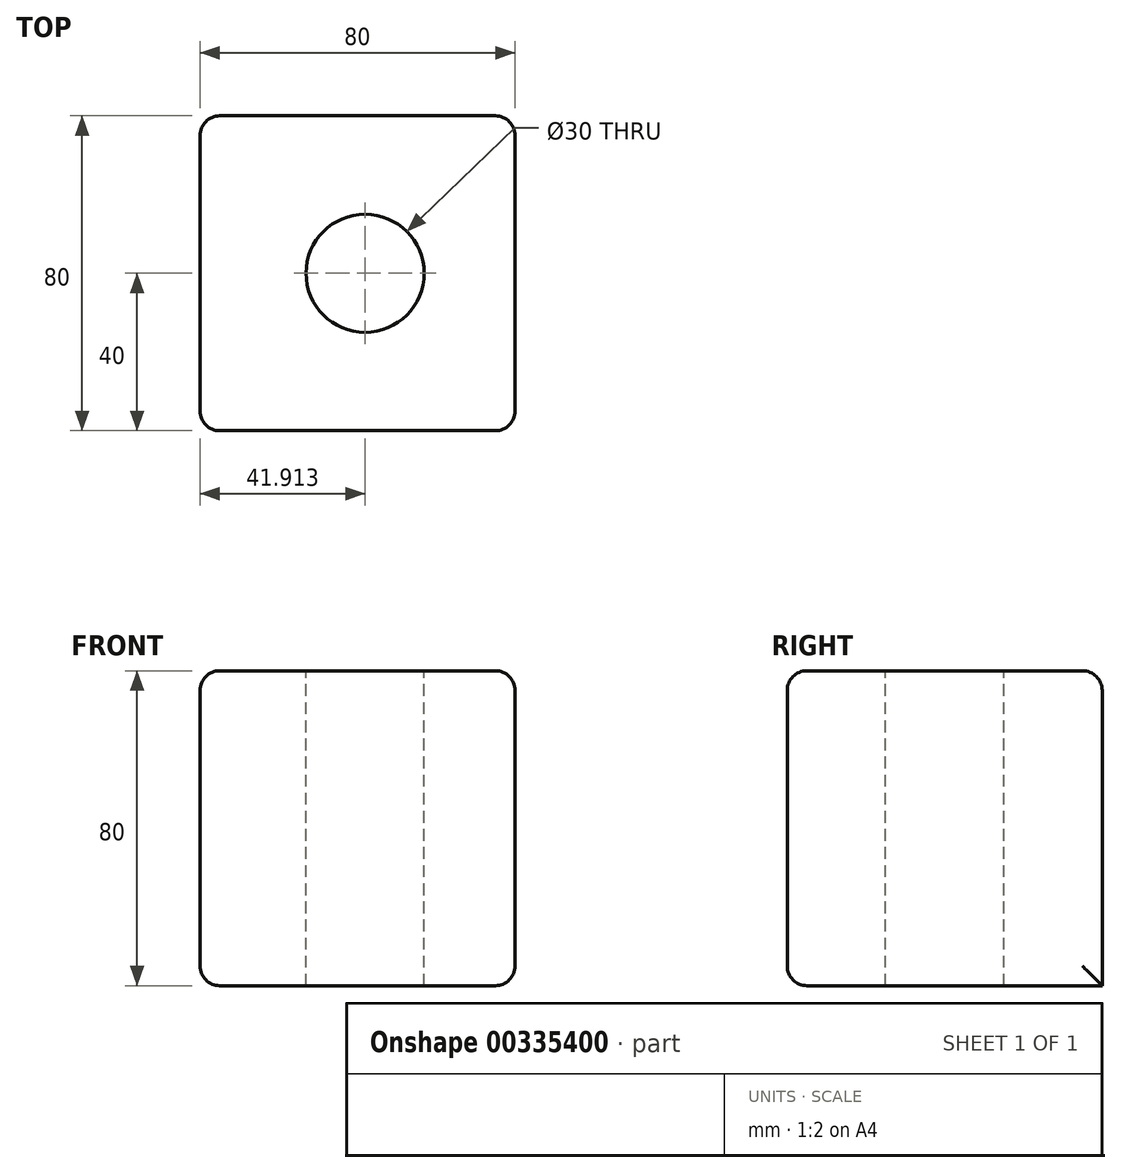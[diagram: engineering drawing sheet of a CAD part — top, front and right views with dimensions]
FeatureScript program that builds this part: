
annotation { "Feature Type Name" : "Feature", "Feature Type Description" : "" }
export const myFeature = defineFeature(function(context is Context, id is Id, definition is map)
    precondition{}
    {
        {
            var Q0;
            Q0=qCreatedBy(makeId("Top.planeOp"),FACE);
            var sketch = newSketch(context, id + "F0", { "sketchPlane" : qUnion([Q0])});
            skLineSegment(sketch, "E0.bottom", {"start": v(40, -40) * mm, "end": v(-40, -40) * mm});
            skLineSegment(sketch, "E0.top", {"start": v(40, 40) * mm, "end": v(-40, 40) * mm});
            skLineSegment(sketch, "E0.left", {"start": v(40, -40) * mm, "end": v(40, 40) * mm});
            skLineSegment(sketch, "E0.right", {"start": v(-40, -40) * mm, "end": v(-40, 40) * mm});
            skPoint(sketch, "E0.middle", {"position": v(0, 0) * mm});
            skSolve(sketch);
        }
        {
            var Q0;
            Q0=makeQuery(id+"F0.imprint","IMPRINT",FACE,{"disambiguationData":[TD([[makeQuery(id+"F0.imprint","IMPRINT",EDGE,{"derivedFrom":sQuery(id+"F0.wireOp",EDGE,"E0.bottom")}),-1.0]])]});
            extrude(context, id + "F1", {"entities" : qUnion([Q0]), "endBound" : BoundingType.SYMMETRIC, "depth" : 80 * mm});
        }
        {
            var Q0;
            Q0=makeQuery(id+"F1.opExtrude","CAP_EDGE",EDGE,{"disambiguationData":[OSD([sQuery(id+"F0.wireOp",EDGE,"E0.right")])],"isStart":false});
            var Q1;
            Q1=makeQuery(id+"F1.opExtrude","CAP_EDGE",EDGE,{"disambiguationData":[OSD([sQuery(id+"F0.wireOp",EDGE,"E0.right")])],"isStart":true});
            var Q2;
            Q2=makeQuery(id+"F1.opExtrude","CAP_EDGE",EDGE,{"disambiguationData":[OSD([sQuery(id+"F0.wireOp",EDGE,"E0.top")])],"isStart":false});
            var Q3;
            Q3=makeQuery(id+"F1.opExtrude","CAP_EDGE",EDGE,{"disambiguationData":[OSD([sQuery(id+"F0.wireOp",EDGE,"E0.bottom")])],"isStart":false});
            var Q4;
            Q4=makeQuery(id+"F1.opExtrude","SWEPT_FACE",FACE,{"disambiguationData":[OSD([sQuery(id+"F0.wireOp",EDGE,"E0.right")])]});
            var Q5;
            Q5=makeQuery(id+"F1.opExtrude","SWEPT_EDGE",EDGE,{"disambiguationData":[OSD([sQuery(id+"F0.wireOp",EDGE,"E0.bottom"),sQuery(id+"F0.wireOp",EDGE,"E0.right")])]});
            var Q6;
            Q6=makeQuery(id+"F1.opExtrude","SWEPT_EDGE",EDGE,{"disambiguationData":[OSD([sQuery(id+"F0.wireOp",EDGE,"E0.top"),sQuery(id+"F0.wireOp",EDGE,"E0.right")])]});
            var Q7;
            Q7=makeQuery(id+"F1.opExtrude","CAP_EDGE",EDGE,{"disambiguationData":[OSD([sQuery(id+"F0.wireOp",EDGE,"E0.left")])],"isStart":true});
            var Q8;
            Q8=makeQuery(id+"F1.opExtrude","SWEPT_EDGE",EDGE,{"disambiguationData":[OSD([sQuery(id+"F0.wireOp",EDGE,"E0.top"),sQuery(id+"F0.wireOp",EDGE,"E0.left")])]});
            var Q9;
            Q9=makeQuery(id+"F1.opExtrude","SWEPT_EDGE",EDGE,{"disambiguationData":[OSD([sQuery(id+"F0.wireOp",EDGE,"E0.bottom"),sQuery(id+"F0.wireOp",EDGE,"E0.left")])]});
            var Q10;
            Q10=makeQuery(id+"F1.opExtrude","CAP_EDGE",EDGE,{"disambiguationData":[OSD([sQuery(id+"F0.wireOp",EDGE,"E0.bottom")])],"isStart":true});
            var Q11;
            Q11=makeQuery(id+"F1.opExtrude","SWEPT_FACE",FACE,{"disambiguationData":[OSD([sQuery(id+"F0.wireOp",EDGE,"E0.left")])]});
            fillet(context, id + "F2", {"entities" : qUnion([Q0, Q1, Q2, Q3, Q4, Q5, Q6, Q7, Q8, Q9, Q10, Q11]), "radius" : 5 * mm, "tangentPropagation" : true, "allowEdgeOverflow" : false});
        }
        {
            var Q0;
            Q0=makeQuery(id+"F1.opExtrude","CAP_FACE",FACE,{"disambiguationData":[OSD([sQuery(id+"F0.wireOp",EDGE,"E0.bottom"),sQuery(id+"F0.wireOp",EDGE,"E0.top"),sQuery(id+"F0.wireOp",EDGE,"E0.left"),sQuery(id+"F0.wireOp",EDGE,"E0.right")])],"isStart":false});
            var sketch = newSketch(context, id + "F3", { "sketchPlane" : qUnion([Q0])});
            skCircle(sketch, "E1", {"center": v(1.91, 0) * mm, "radius": 15 * mm});
            skSolve(sketch);
        }
        {
            var Q0;
            Q0 = qSketchRegion(id + "F3", true);
            extrude(context, id + "F4", {"entities" : qUnion([Q0]), "operationType" : NewBodyOperationType.REMOVE, "endBound" : BoundingType.THROUGH_ALL, "oppositeDirection" : true, "depth" : 25 * mm});
        }
    });
